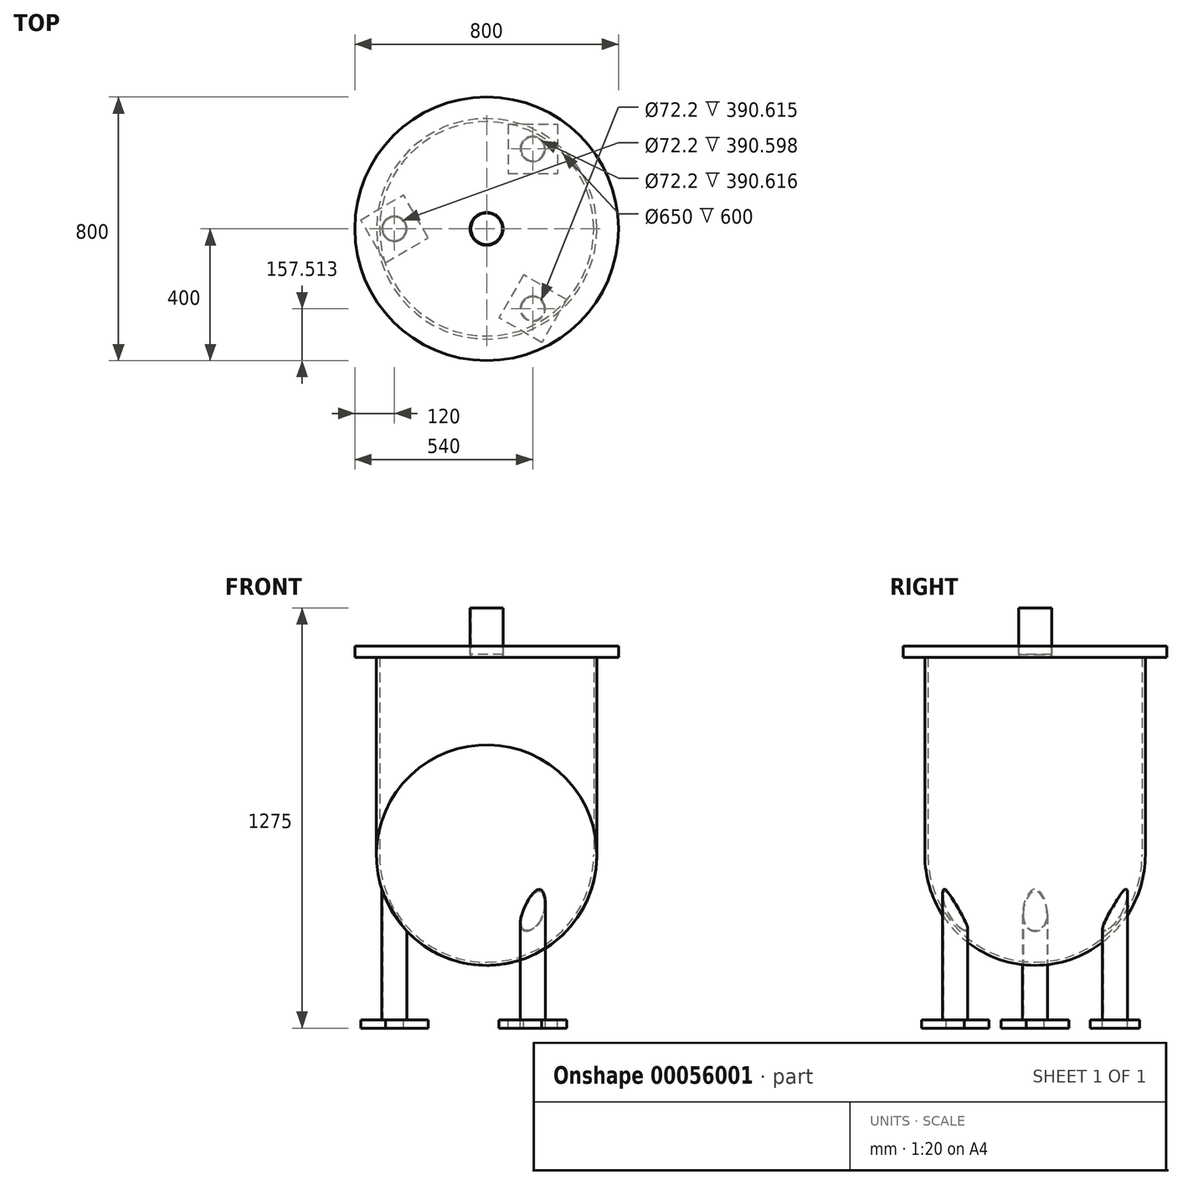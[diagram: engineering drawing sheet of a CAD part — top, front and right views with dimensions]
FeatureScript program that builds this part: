
annotation { "Feature Type Name" : "Feature", "Feature Type Description" : "" }
export const myFeature = defineFeature(function(context is Context, id is Id, definition is map)
    precondition{}
    {
        {
            var Q0;
            Q0=qCreatedBy(makeId("Front.planeOp"),FACE);
            var sketch = newSketch(context, id + "F0", { "sketchPlane" : qUnion([Q0])});
            skLineSegment(sketch, "E0", {"start": v(0, 0) * mm, "end": v(0, 600) * mm, "construction": true});
            skArc(sketch, "E1", {"start": v(-325, 0) * mm, "mid": v(-229.8, -229.8) * mm, "end": v(0, -325) * mm});
            skLineSegment(sketch, "E2", {"start": v(-325, 0) * mm, "end": v(-325, 600) * mm});
            skLineSegment(sketch, "E3.0", {"start": v(-334.5, 0) * mm, "end": v(-334.5, 600) * mm});
            skArc(sketch, "E3.1", {"start": v(-334.5, 0) * mm, "mid": v(-236.53, -236.53) * mm, "end": v(0, -334.5) * mm});
            skLineSegment(sketch, "E4", {"start": v(-334.5, 600) * mm, "end": v(-325, 600) * mm});
            skLineSegment(sketch, "E5", {"start": v(0, -334.5) * mm, "end": v(0, -325) * mm});
            skLineSegment(sketch, "E6", {"start": v(0, 600) * mm, "end": v(-325, 600) * mm});
            skLineSegment(sketch, "E7", {"start": v(-334.5, 600) * mm, "end": v(-400, 600) * mm});
            skLineSegment(sketch, "E8", {"start": v(-400, 600) * mm, "end": v(-400, 634) * mm});
            skLineSegment(sketch, "E9", {"start": v(-400, 634) * mm, "end": v(0, 634) * mm});
            skLineSegment(sketch, "E10", {"start": v(0, 634) * mm, "end": v(0, 600) * mm});
            skSolve(sketch);
        }
        {
            var Q0;
            Q0 = qSketchRegion(id + "F0", true);
            var Q1;
            Q1=sQuery(id+"F0.wireOp",EDGE,"E0");
            revolve(context, id + "F1", {"entities" : qUnion([Q0]), "axis" : qUnion([Q1]), "revolveType" : RevolveType.FULL});
        }
        {
            var Q0;
            Q0=makeQuery(id+"F1.opRevolve","SWEPT_FACE",FACE,{"disambiguationData":[OSD([sQuery(id+"F0.wireOp",EDGE,"E9")])]});
            var sketch = newSketch(context, id + "F2", { "sketchPlane" : qUnion([Q0])});
            skCircle(sketch, "E11", {"center": v(0, 0) * mm, "radius": 50 * mm});
            skSolve(sketch);
        }
        {
            var Q0;
            Q0 = qSketchRegion(id + "F2", true);
            extrude(context, id + "F3", {"entities" : qUnion([Q0]), "operationType" : NewBodyOperationType.REMOVE, "oppositeDirection" : true, "depth" : 25 * mm});
        }
        {
            var Q0;
            Q0=makeQuery(id+"F1.opRevolve","SWEPT_FACE",FACE,{"disambiguationData":[OSD([sQuery(id+"F0.wireOp",EDGE,"E7")])]});
            var sketch = newSketch(context, id + "F4", { "sketchPlane" : qUnion([Q0])});
            skCircle(sketch, "E12.0", {"center": v(0, 0) * mm, "radius": 50 * mm});
            skCircle(sketch, "E13", {"center": v(0, 0) * mm, "radius": 48 * mm});
            skSolve(sketch);
        }
        {
            var Q0;
            Q0 = qSketchRegion(id + "F4", true);
            extrude(context, id + "F5", {"entities" : qUnion([Q0]), "oppositeDirection" : true, "depth" : 150 * mm});
        }
        {
            var Q0;
            Q0=makeQuery(id+"F5.opExtrude","CAP_FACE",FACE,{"disambiguationData":[OSD([sQuery(id+"F4.wireOp",EDGE,"E12.0"),sQuery(id+"F4.wireOp",EDGE,"E13")])],"isStart":false});
            var sketch = newSketch(context, id + "F6", { "sketchPlane" : qUnion([Q0])});
            skCircle(sketch, "E14.0", {"center": v(0, 0) * mm, "radius": 50 * mm});
            skCircle(sketch, "E15", {"center": v(0, 0) * mm, "radius": 75 * mm});
            skCircle(sketch, "E16", {"center": v(0, 60) * mm, "radius": 6.35 * mm});
            skLineSegment(sketch, "E17", {"start": v(0, 60) * mm, "end": v(0, 0) * mm, "construction": true});
            skCircle(sketch, "E18.1.0", {"center": v(-60, 0) * mm, "radius": 6.35 * mm});
            skCircle(sketch, "E18.2.0", {"center": v(0, -60) * mm, "radius": 6.35 * mm});
            skCircle(sketch, "E18.3.0", {"center": v(60, 0) * mm, "radius": 6.35 * mm});
            skSolve(sketch);
        }
        {
            var Q0;
            Q0=makeQuery(id+"F6.imprint","IMPRINT",FACE,{"disambiguationData":[TD([[makeQuery(id+"F6.imprint","IMPRINT",EDGE,{"derivedFrom":sQuery(id+"F6.wireOp",EDGE,"E14.0")}),-1.0]])]});
            extrude(context, id + "F7", {"entities" : qUnion([Q0]), "operationType" : NewBodyOperationType.ADD, "oppositeDirection" : true, "depth" : 25 * mm});
        }
        {
            var Q0;
            Q0=qCreatedBy(makeId("Top.planeOp"),FACE);
            cPlane(context, id + "F8", {"entities" : qUnion([Q0]), "cplaneType" : CPlaneType.OFFSET, "offset" : 500 * mm, "oppositeDirection" : true, "width" : 150 * mm, "height" : 150 * mm});
        }
        {
            var Q0;
            Q0=qCreatedBy(id+"F8.planeOp",FACE);
            var sketch = newSketch(context, id + "F9", { "sketchPlane" : qUnion([Q0])});
            skCircle(sketch, "E19", {"center": v(-280, 0) * mm, "radius": 38.1 * mm});
            skLineSegment(sketch, "E20", {"start": v(0, 0) * mm, "end": v(-280, 0) * mm, "construction": true});
            skCircle(sketch, "E21", {"center": v(-280, 0) * mm, "radius": 36.1 * mm});
            skCircle(sketch, "E22.1.0", {"center": v(140, -242.49) * mm, "radius": 36.1 * mm});
            skCircle(sketch, "E22.1.1", {"center": v(140, -242.49) * mm, "radius": 38.1 * mm});
            skCircle(sketch, "E22.2.0", {"center": v(140, 242.49) * mm, "radius": 36.1 * mm});
            skCircle(sketch, "E22.2.1", {"center": v(140, 242.49) * mm, "radius": 38.1 * mm});
            skPoint(sketch, "E22.center", {"position": v(0, 0) * mm});
            skSolve(sketch);
        }
        {
            var Q0;
            Q0=makeQuery(id+"F9.imprint","IMPRINT",FACE,{"disambiguationData":[TD([[makeQuery(id+"F9.imprint","IMPRINT",EDGE,{"derivedFrom":sQuery(id+"F9.wireOp",EDGE,"E22.2.0")}),-1.0]])]});
            var Q1;
            Q1=makeQuery(id+"F9.imprint","IMPRINT",FACE,{"disambiguationData":[TD([[makeQuery(id+"F9.imprint","IMPRINT",EDGE,{"derivedFrom":sQuery(id+"F9.wireOp",EDGE,"E19")}),1.0]])]});
            var Q2;
            Q2=makeQuery(id+"F9.imprint","IMPRINT",FACE,{"disambiguationData":[TD([[makeQuery(id+"F9.imprint","IMPRINT",EDGE,{"derivedFrom":sQuery(id+"F9.wireOp",EDGE,"E22.1.0")}),-1.0]])]});
            extrude(context, id + "F10", {"entities" : qUnion([Q0, Q1, Q2]), "endBound" : BoundingType.UP_TO_NEXT, "depth" : 25 * mm});
        }
        {
            var Q0;
            Q0=makeQuery(id+"F10.opExtrude","CAP_FACE",FACE,{"disambiguationData":[OSD([sQuery(id+"F9.wireOp",EDGE,"E22.2.0"),sQuery(id+"F9.wireOp",EDGE,"E22.2.1")])],"isStart":true});
            var sketch = newSketch(context, id + "F11", { "sketchPlane" : qUnion([Q0])});
            skLineSegment(sketch, "E23.rect.bottom", {"start": v(65, -317.49) * mm, "end": v(215, -317.49) * mm});
            skLineSegment(sketch, "E23.rect.top", {"start": v(65, -167.49) * mm, "end": v(215, -167.49) * mm});
            skLineSegment(sketch, "E23.rect.left", {"start": v(65, -317.49) * mm, "end": v(65, -167.49) * mm});
            skLineSegment(sketch, "E23.rect.right", {"start": v(215, -317.49) * mm, "end": v(215, -167.49) * mm});
            skPoint(sketch, "E23.rect.middle", {"position": v(140, -242.49) * mm});
            skLineSegment(sketch, "E24.1.0", {"start": v(112.55, 140.04) * mm, "end": v(37.55, 269.94) * mm});
            skLineSegment(sketch, "E24.1.1", {"start": v(167.45, 344.94) * mm, "end": v(37.55, 269.94) * mm});
            skLineSegment(sketch, "E24.1.2", {"start": v(242.45, 215.04) * mm, "end": v(167.45, 344.94) * mm});
            skLineSegment(sketch, "E24.1.3", {"start": v(242.45, 215.04) * mm, "end": v(112.55, 140.04) * mm});
            skLineSegment(sketch, "E24.2.0", {"start": v(-177.55, 27.45) * mm, "end": v(-252.55, -102.45) * mm});
            skLineSegment(sketch, "E24.2.1", {"start": v(-382.45, -27.45) * mm, "end": v(-252.55, -102.45) * mm});
            skLineSegment(sketch, "E24.2.2", {"start": v(-307.45, 102.45) * mm, "end": v(-382.45, -27.45) * mm});
            skLineSegment(sketch, "E24.2.3", {"start": v(-307.45, 102.45) * mm, "end": v(-177.55, 27.45) * mm});
            skPoint(sketch, "E24.center", {"position": v(0, 0) * mm});
            skSolve(sketch);
        }
        {
            var Q0;
            Q0=makeQuery(id+"F11.imprint","IMPRINT",FACE,{"disambiguationData":[TD([[makeQuery(id+"F11.imprint","IMPRINT",EDGE,{"derivedFrom":sQuery(id+"F11.wireOp",EDGE,"E24.2.0")}),-1.0]])]});
            var Q1;
            Q1=makeQuery(id+"F11.imprint","IMPRINT",FACE,{"disambiguationData":[TD([[makeQuery(id+"F11.imprint","IMPRINT",EDGE,{"derivedFrom":sQuery(id+"F11.wireOp",EDGE,"E24.1.0")}),-1.0]])]});
            var Q2;
            Q2=makeQuery(id+"F11.imprint","IMPRINT",FACE,{"disambiguationData":[TD([[makeQuery(id+"F11.imprint","IMPRINT",EDGE,{"derivedFrom":sQuery(id+"F11.wireOp",EDGE,"E23.rect.bottom")}),1.0]])]});
            extrude(context, id + "F12", {"entities" : qUnion([Q0, Q1, Q2]), "operationType" : NewBodyOperationType.ADD, "depth" : 25 * mm});
        }
    });
